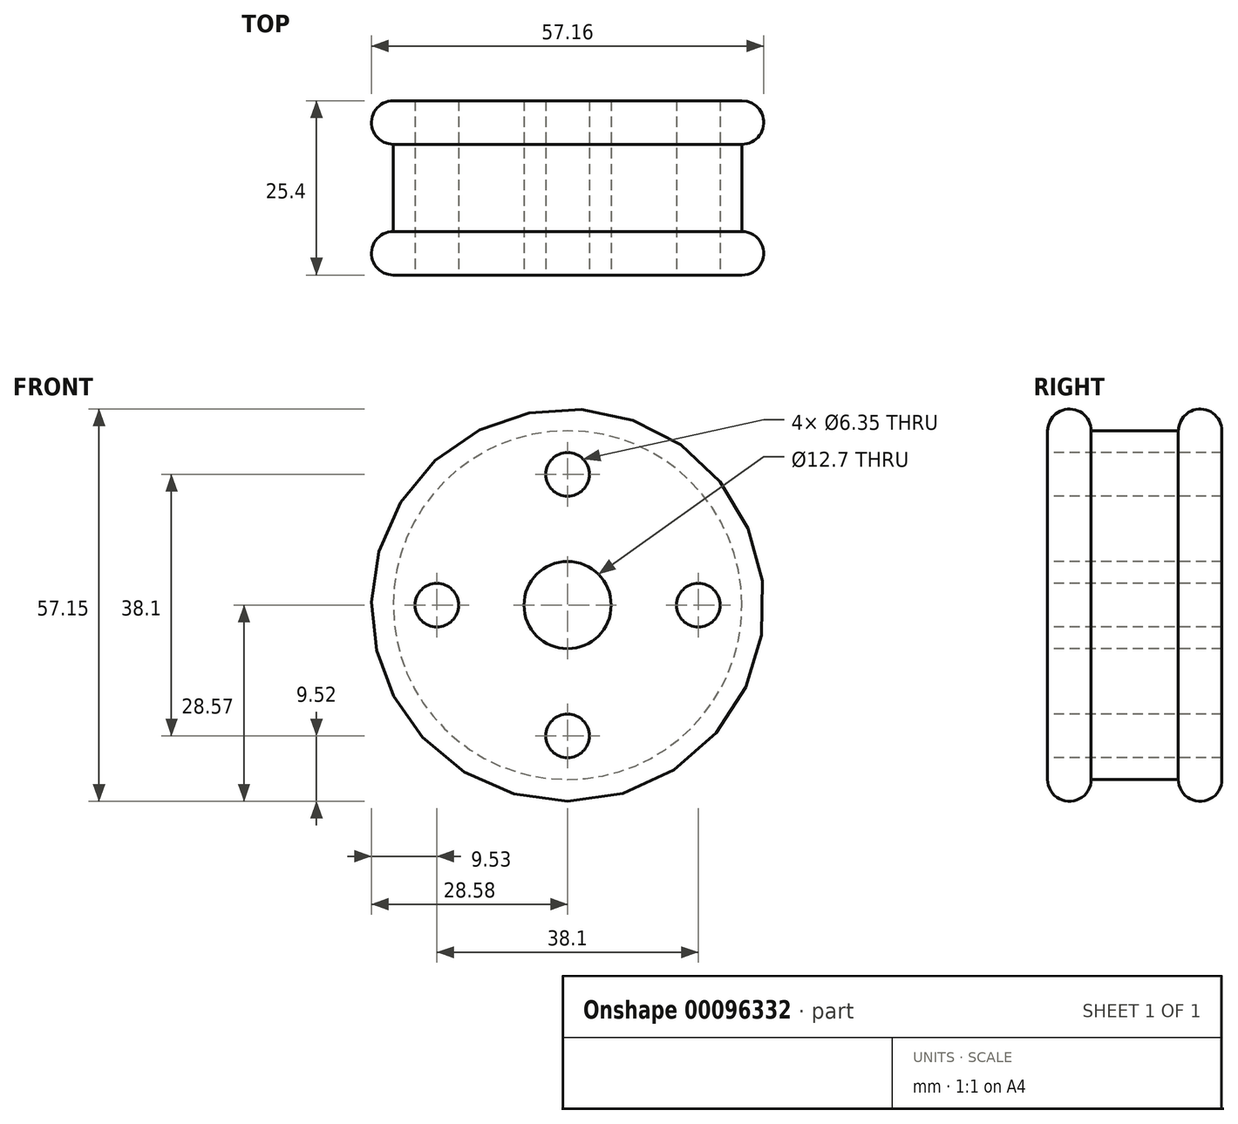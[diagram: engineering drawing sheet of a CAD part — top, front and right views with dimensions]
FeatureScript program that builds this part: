
annotation { "Feature Type Name" : "Feature", "Feature Type Description" : "" }
export const myFeature = defineFeature(function(context is Context, id is Id, definition is map)
    precondition{}
    {
        {
            var Q0;
            Q0=qCreatedBy(makeId("Front.planeOp"),FACE);
            var sketch = newSketch(context, id + "F0", { "sketchPlane" : qUnion([Q0])});
            skCircle(sketch, "E0", {"center": v(0, 0) * mm, "radius": 28.57 * mm});
            skSolve(sketch);
        }
        {
            var Q0;
            Q0 = qSketchRegion(id + "F0", true);
            extrude(context, id + "F1", {"entities" : qUnion([Q0]), "depth" : 6.35 * mm});
        }
        {
            var Q0;
            Q0=makeQuery(id+"F1.opExtrude","SWEPT_FACE",FACE,{"disambiguationData":[OSD([sQuery(id+"F0.wireOp",EDGE,"E0")])]});
            fillet(context, id + "F2", {"entities" : qUnion([Q0]), "radius" : 3.17 * mm, "tangentPropagation" : true, "allowEdgeOverflow" : false});
        }
        {
            var Q0;
            Q0=makeQuery(id+"F1.opExtrude","CAP_FACE",FACE,{"disambiguationData":[OSD([sQuery(id+"F0.wireOp",EDGE,"E0")])],"isStart":false});
            var sketch = newSketch(context, id + "F3", { "sketchPlane" : qUnion([Q0])});
            skCircle(sketch, "E1", {"center": v(0, 0) * mm, "radius": 25.4 * mm});
            skSolve(sketch);
        }
        {
            var Q0;
            Q0 = qSketchRegion(id + "F3", true);
            extrude(context, id + "F4", {"entities" : qUnion([Q0]), "operationType" : NewBodyOperationType.ADD, "depth" : 12.7 * mm});
        }
        {
            var Q0;
            Q0=makeQuery(id+"F4.opExtrude","CAP_FACE",FACE,{"disambiguationData":[OSD([sQuery(id+"F3.wireOp",EDGE,"E1")])],"isStart":false});
            var sketch = newSketch(context, id + "F5", { "sketchPlane" : qUnion([Q0])});
            skCircle(sketch, "E2", {"center": v(0, 0) * mm, "radius": 28.57 * mm});
            skSolve(sketch);
        }
        {
            var Q0;
            Q0 = qSketchRegion(id + "F5", true);
            extrude(context, id + "F6", {"entities" : qUnion([Q0]), "operationType" : NewBodyOperationType.ADD, "depth" : 6.35 * mm});
        }
        {
            var Q0;
            Q0=makeQuery(id+"F6.opExtrude","SWEPT_FACE",FACE,{"disambiguationData":[OSD([sQuery(id+"F5.wireOp",EDGE,"E2")])]});
            fillet(context, id + "F7", {"entities" : qUnion([Q0]), "radius" : 3.17 * mm, "tangentPropagation" : true, "allowEdgeOverflow" : false});
        }
        {
            var Q0;
            Q0=makeQuery(id+"F6.opExtrude","CAP_FACE",FACE,{"disambiguationData":[OSD([sQuery(id+"F5.wireOp",EDGE,"E2")])],"isStart":false});
            var sketch = newSketch(context, id + "F8", { "sketchPlane" : qUnion([Q0])});
            skCircle(sketch, "E3", {"center": v(0, 0) * mm, "radius": 6.35 * mm});
            skCircle(sketch, "E4", {"center": v(0, 19.05) * mm, "radius": 3.18 * mm});
            skCircle(sketch, "E5", {"center": v(-19.05, 0) * mm, "radius": 3.18 * mm});
            skCircle(sketch, "E6", {"center": v(19.05, 0) * mm, "radius": 3.18 * mm});
            skCircle(sketch, "E7", {"center": v(0, -19.05) * mm, "radius": 3.18 * mm});
            skSolve(sketch);
        }
        {
            var Q0;
            Q0 = qSketchRegion(id + "F8", true);
            extrude(context, id + "F9", {"entities" : qUnion([Q0]), "operationType" : NewBodyOperationType.REMOVE, "endBound" : BoundingType.THROUGH_ALL, "oppositeDirection" : true, "depth" : 25.4 * mm});
        }
    });
